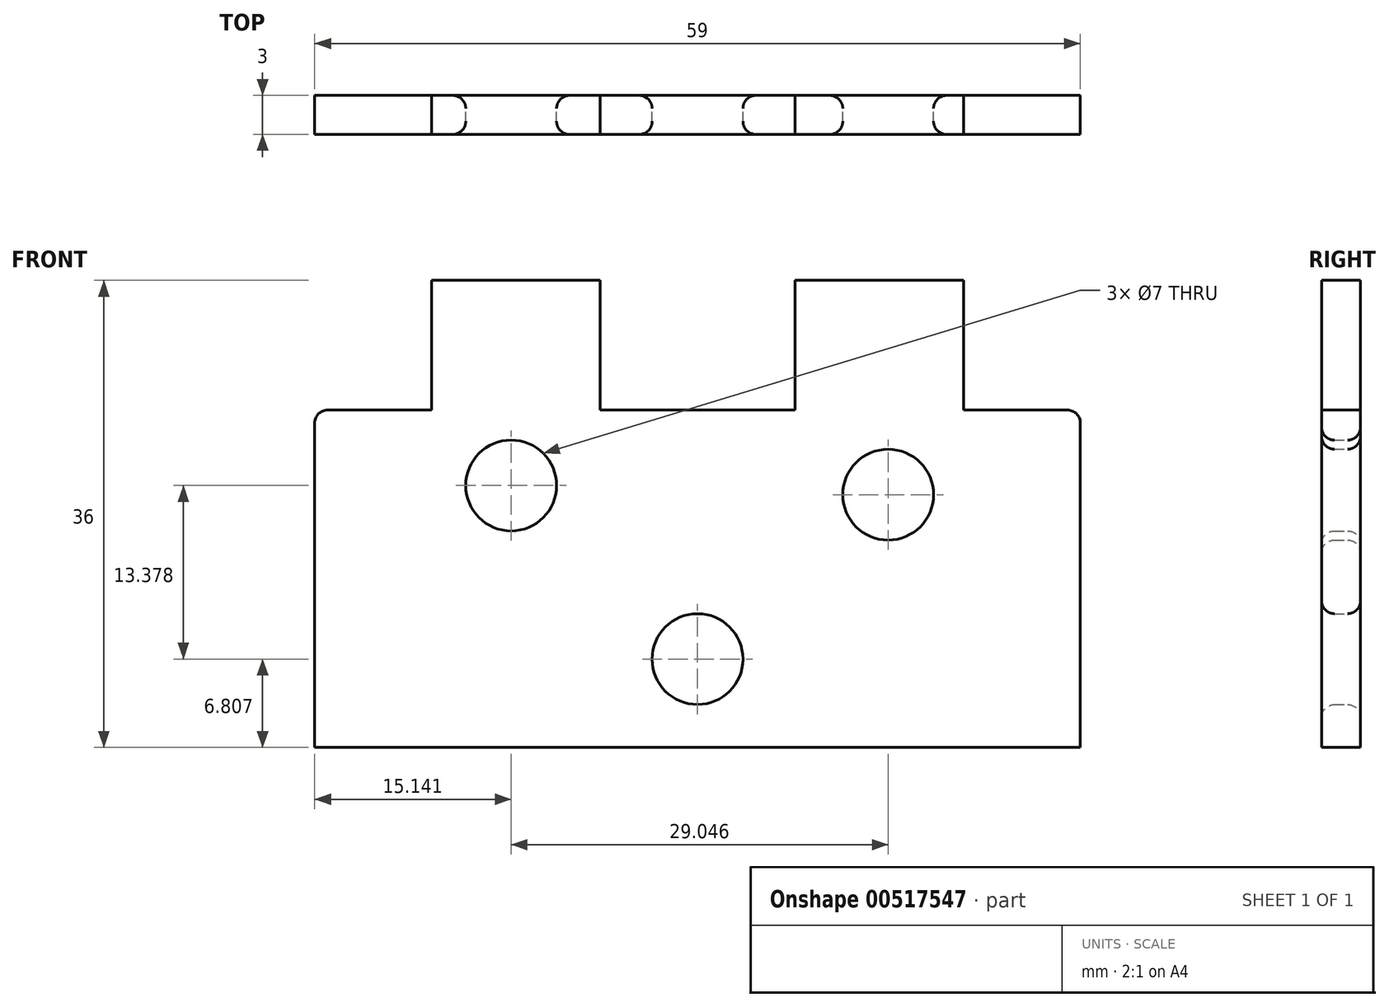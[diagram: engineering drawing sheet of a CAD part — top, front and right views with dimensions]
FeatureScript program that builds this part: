
annotation { "Feature Type Name" : "Feature", "Feature Type Description" : "" }
export const myFeature = defineFeature(function(context is Context, id is Id, definition is map)
    precondition{}
    {
        {
            var Q0;
            Q0=qCreatedBy(makeId("Front.planeOp"),FACE);
            var sketch = newSketch(context, id + "F0", { "sketchPlane" : qUnion([Q0])});
            skLineSegment(sketch, "E0.bottom", {"start": v(29.5, -13) * mm, "end": v(-29.5, -13) * mm});
            skLineSegment(sketch, "E0.top", {"start": v(29.5, 13) * mm, "end": v(-29.5, 13) * mm});
            skLineSegment(sketch, "E0.left", {"start": v(29.5, -13) * mm, "end": v(29.5, 13) * mm});
            skLineSegment(sketch, "E0.right", {"start": v(-29.5, -13) * mm, "end": v(-29.5, 13) * mm});
            skPoint(sketch, "E0.middle", {"position": v(0, 0) * mm});
            skLineSegment(sketch, "E1.bottom", {"start": v(-7.5, 13) * mm, "end": v(-20.5, 13) * mm});
            skLineSegment(sketch, "E1.top", {"start": v(-7.5, 23) * mm, "end": v(-20.5, 23) * mm});
            skLineSegment(sketch, "E1.left", {"start": v(-7.5, 13) * mm, "end": v(-7.5, 23) * mm});
            skLineSegment(sketch, "E1.right", {"start": v(-20.5, 13) * mm, "end": v(-20.5, 23) * mm});
            skPoint(sketch, "E1.middle", {"position": v(-14, 18) * mm});
            skLineSegment(sketch, "E2.bottom", {"start": v(20.5, 13) * mm, "end": v(7.5, 13) * mm});
            skLineSegment(sketch, "E2.top", {"start": v(20.5, 23) * mm, "end": v(7.5, 23) * mm});
            skLineSegment(sketch, "E2.left", {"start": v(20.5, 13) * mm, "end": v(20.5, 23) * mm});
            skLineSegment(sketch, "E2.right", {"start": v(7.5, 13) * mm, "end": v(7.5, 23) * mm});
            skPoint(sketch, "E2.middle", {"position": v(14, 18) * mm});
            skCircle(sketch, "E3", {"center": v(0, -6.2) * mm, "radius": 3.5 * mm});
            skCircle(sketch, "E4", {"center": v(14.69, 6.48) * mm, "radius": 3.5 * mm});
            skCircle(sketch, "E5", {"center": v(-14.36, 7.19) * mm, "radius": 3.5 * mm});
            skSolve(sketch);
        }
        {
            var Q0;
            Q0 = qSketchRegion(id + "F0", true);
            extrude(context, id + "F1", {"entities" : qUnion([Q0]), "endBound" : BoundingType.SYMMETRIC, "depth" : 3 * mm, "offsetDistance" : 25 * mm});
        }
        {
            var Q0;
            Q0=makeQuery(id+"F1.opExtrude","SWEPT_EDGE",EDGE,{"disambiguationData":[OSD([sQuery(id+"F0.wireOp",EDGE,"E0.top"),sQuery(id+"F0.wireOp",EDGE,"E0.right")])]});
            var Q1;
            Q1=makeQuery(id+"F1.opExtrude","SWEPT_EDGE",EDGE,{"disambiguationData":[OSD([sQuery(id+"F0.wireOp",EDGE,"E0.top"),sQuery(id+"F0.wireOp",EDGE,"E0.left")])]});
            var Q2;
            Q2=makeQuery(id+"F1.opExtrude","CAP_EDGE",EDGE,{"disambiguationData":[OSD([sQuery(id+"F0.wireOp",EDGE,"E5")])],"isStart":false});
            var Q3;
            Q3=makeQuery(id+"F1.opExtrude","CAP_EDGE",EDGE,{"disambiguationData":[OSD([sQuery(id+"F0.wireOp",EDGE,"E4")])],"isStart":false});
            var Q4;
            Q4=makeQuery(id+"F1.opExtrude","CAP_EDGE",EDGE,{"disambiguationData":[OSD([sQuery(id+"F0.wireOp",EDGE,"E3")])],"isStart":false});
            fillet(context, id + "F2", {"entities" : qUnion([Q0, Q1, Q2, Q3, Q4]), "radius" : 1 * mm, "tangentPropagation" : true, "allowEdgeOverflow" : false});
        }
        {
            var Q0;
            Q0=makeQuery(id+"F1.opExtrude","CAP_EDGE",EDGE,{"disambiguationData":[OSD([sQuery(id+"F0.wireOp",EDGE,"E4")])],"isStart":true});
            var Q1;
            Q1=makeQuery(id+"F1.opExtrude","CAP_EDGE",EDGE,{"disambiguationData":[OSD([sQuery(id+"F0.wireOp",EDGE,"E5")])],"isStart":true});
            var Q2;
            Q2=makeQuery(id+"F1.opExtrude","CAP_EDGE",EDGE,{"disambiguationData":[OSD([sQuery(id+"F0.wireOp",EDGE,"E3")])],"isStart":true});
            fillet(context, id + "F3", {"entities" : qUnion([Q0, Q1, Q2]), "radius" : 1 * mm, "tangentPropagation" : true, "allowEdgeOverflow" : false});
        }
    });
